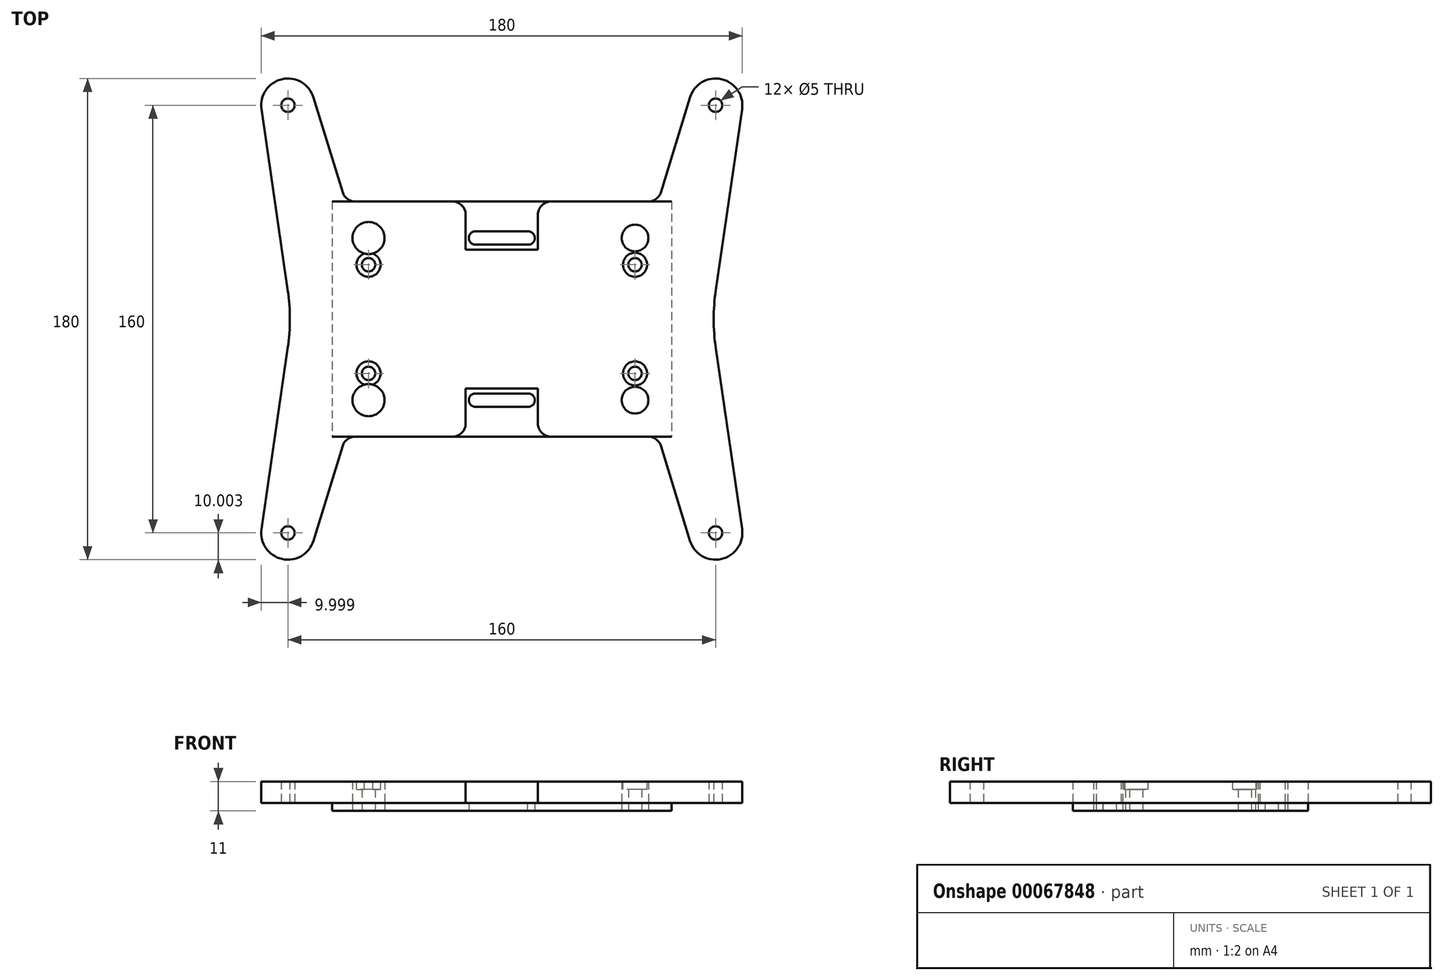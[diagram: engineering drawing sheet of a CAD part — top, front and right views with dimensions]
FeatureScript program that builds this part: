
annotation { "Feature Type Name" : "Feature", "Feature Type Description" : "" }
export const myFeature = defineFeature(function(context is Context, id is Id, definition is map)
    precondition{}
    {
        {
            var Q0;
            Q0=qCreatedBy(makeId("Top.planeOp"),FACE);
            var sketch = newSketch(context, id + "F0", { "sketchPlane" : qUnion([Q0])});
            skLineSegment(sketch, "E0.bottom", {"start": v(-92.69, 30.95) * mm, "end": v(34.32, 30.95) * mm});
            skLineSegment(sketch, "E0.top", {"start": v(-92.69, -57.05) * mm, "end": v(34.32, -57.05) * mm});
            skLineSegment(sketch, "E0.left", {"start": v(-92.69, 30.95) * mm, "end": v(-92.69, -57.05) * mm});
            skLineSegment(sketch, "E0.right", {"start": v(34.32, 30.95) * mm, "end": v(34.32, -57.05) * mm});
            skLineSegment(sketch, "E1", {"start": v(-79.03, 30.95) * mm, "end": v(-79.03, -57.05) * mm, "construction": true});
            skLineSegment(sketch, "E2", {"start": v(20.67, 30.95) * mm, "end": v(20.67, -57.05) * mm, "construction": true});
            skLineSegment(sketch, "E3", {"start": v(-92.69, 17.28) * mm, "end": v(34.32, 17.28) * mm, "construction": true});
            skLineSegment(sketch, "E4", {"start": v(-92.69, -43.37) * mm, "end": v(34.32, -43.37) * mm, "construction": true});
            skLineSegment(sketch, "E5", {"start": v(-92.69, -33.37) * mm, "end": v(34.32, -33.37) * mm, "construction": true});
            skLineSegment(sketch, "E6", {"start": v(-92.69, 7.28) * mm, "end": v(34.32, 7.28) * mm, "construction": true});
            skCircle(sketch, "E7", {"center": v(-79.03, 17.28) * mm, "radius": 6 * mm});
            skCircle(sketch, "E8", {"center": v(20.67, 17.28) * mm, "radius": 5 * mm});
            skCircle(sketch, "E9", {"center": v(20.67, 7.28) * mm, "radius": 2.5 * mm});
            skCircle(sketch, "E10", {"center": v(-79.03, 7.28) * mm, "radius": 2.5 * mm});
            skCircle(sketch, "E11", {"center": v(-79.03, -33.37) * mm, "radius": 2.5 * mm});
            skCircle(sketch, "E12", {"center": v(20.67, -33.37) * mm, "radius": 2.5 * mm});
            skCircle(sketch, "E13", {"center": v(20.67, -43.37) * mm, "radius": 5 * mm});
            skCircle(sketch, "E14", {"center": v(-79.03, -43.37) * mm, "radius": 6 * mm});
            skArc(sketch, "E15", {"start": v(-39.03, -40.87) * mm, "mid": v(-41.53, -43.37) * mm, "end": v(-39.02, -45.87) * mm});
            skArc(sketch, "E16", {"start": v(-19.68, -45.84) * mm, "mid": v(-16.83, -43.54) * mm, "end": v(-19.33, -40.87) * mm});
            skLineSegment(sketch, "E17", {"start": v(-39.03, -40.87) * mm, "end": v(-19.33, -40.87) * mm});
            skLineSegment(sketch, "E18", {"start": v(-18.97, -45.84) * mm, "end": v(-39.02, -45.87) * mm});
            skArc(sketch, "E19", {"start": v(-39.03, 19.78) * mm, "mid": v(-41.53, 17.28) * mm, "end": v(-39.03, 14.78) * mm});
            skArc(sketch, "E20", {"start": v(-19.33, 14.78) * mm, "mid": v(-16.83, 17.28) * mm, "end": v(-19.33, 19.78) * mm});
            skLineSegment(sketch, "E21", {"start": v(-39.03, 19.78) * mm, "end": v(-19.33, 19.78) * mm});
            skLineSegment(sketch, "E22", {"start": v(-39.03, 14.78) * mm, "end": v(-19.33, 14.78) * mm});
            skLineSegment(sketch, "E23", {"start": v(-42.69, 30.95) * mm, "end": v(-42.69, -57.05) * mm, "construction": true});
            skLineSegment(sketch, "E24", {"start": v(-15.68, 30.95) * mm, "end": v(-15.68, -57.05) * mm, "construction": true});
            skLineSegment(sketch, "E25", {"start": v(-42.69, 12.95) * mm, "end": v(-15.68, 12.95) * mm, "construction": true});
            skLineSegment(sketch, "E26", {"start": v(-42.69, -39.05) * mm, "end": v(-15.68, -39.05) * mm, "construction": true});
            skSolve(sketch);
        }
        {
            var Q0;
            Q0=makeQuery(id+"F0.imprint","IMPRINT",FACE,{"disambiguationData":[TD([[makeQuery(id+"F0.imprint","IMPRINT",EDGE,{"derivedFrom":sQuery(id+"F0.wireOp",EDGE,"E0.bottom")}),-1.0]])]});
            extrude(context, id + "F1", {"entities" : qUnion([Q0]), "depth" : 3 * mm});
        }
        {
            var Q0;
            Q0=makeQuery(id+"F1.opExtrude","CAP_FACE",FACE,{"disambiguationData":[OSD([sQuery(id+"F0.wireOp",EDGE,"E0.bottom"),sQuery(id+"F0.wireOp",EDGE,"E0.top"),sQuery(id+"F0.wireOp",EDGE,"E0.left"),sQuery(id+"F0.wireOp",EDGE,"E0.right"),sQuery(id+"F0.wireOp",EDGE,"E7"),sQuery(id+"F0.wireOp",EDGE,"E8"),sQuery(id+"F0.wireOp",EDGE,"E9"),sQuery(id+"F0.wireOp",EDGE,"E10"),sQuery(id+"F0.wireOp",EDGE,"E11"),sQuery(id+"F0.wireOp",EDGE,"E12"),sQuery(id+"F0.wireOp",EDGE,"E13"),sQuery(id+"F0.wireOp",EDGE,"E14"),sQuery(id+"F0.wireOp",EDGE,"E15"),sQuery(id+"F0.wireOp",EDGE,"E16"),sQuery(id+"F0.wireOp",EDGE,"E17"),sQuery(id+"F0.wireOp",EDGE,"E18"),sQuery(id+"F0.wireOp",EDGE,"E19"),sQuery(id+"F0.wireOp",EDGE,"E20"),sQuery(id+"F0.wireOp",EDGE,"E21"),sQuery(id+"F0.wireOp",EDGE,"E22")])],"isStart":false});
            var sketch = newSketch(context, id + "F2", { "sketchPlane" : qUnion([Q0])});
            skLineSegment(sketch, "E27.0", {"start": v(-92.69, 30.95) * mm, "end": v(34.32, 30.95) * mm});
            skLineSegment(sketch, "E27.1", {"start": v(-92.69, 30.95) * mm, "end": v(-92.69, -57.05) * mm});
            skLineSegment(sketch, "E27.2", {"start": v(34.32, 30.95) * mm, "end": v(34.32, -57.05) * mm});
            skLineSegment(sketch, "E27.3", {"start": v(-92.69, -57.05) * mm, "end": v(34.32, -57.05) * mm});
            skCircle(sketch, "E27.4", {"center": v(-79.03, -43.37) * mm, "radius": 6 * mm});
            skCircle(sketch, "E27.5", {"center": v(-79.03, -33.37) * mm, "radius": 2.5 * mm});
            skCircle(sketch, "E27.6", {"center": v(-79.03, 7.28) * mm, "radius": 2.5 * mm});
            skCircle(sketch, "E27.7", {"center": v(-79.03, 17.28) * mm, "radius": 6 * mm});
            skCircle(sketch, "E27.8", {"center": v(20.67, 17.28) * mm, "radius": 5 * mm});
            skCircle(sketch, "E27.9", {"center": v(20.67, 7.28) * mm, "radius": 2.5 * mm});
            skCircle(sketch, "E27.10", {"center": v(20.67, -33.37) * mm, "radius": 2.5 * mm});
            skCircle(sketch, "E27.11", {"center": v(20.67, -43.37) * mm, "radius": 5 * mm});
            skLineSegment(sketch, "E28.bottom", {"start": v(-42.69, 30.95) * mm, "end": v(-15.68, 30.95) * mm});
            skLineSegment(sketch, "E28.top", {"start": v(-42.69, 12.95) * mm, "end": v(-15.68, 12.95) * mm});
            skLineSegment(sketch, "E28.left", {"start": v(-42.69, 30.95) * mm, "end": v(-42.69, 12.95) * mm});
            skLineSegment(sketch, "E28.right", {"start": v(-15.68, 30.95) * mm, "end": v(-15.68, 12.95) * mm});
            skLineSegment(sketch, "E29.bottom", {"start": v(-15.68, -57.05) * mm, "end": v(-42.69, -57.05) * mm});
            skLineSegment(sketch, "E29.top", {"start": v(-15.68, -39.05) * mm, "end": v(-42.69, -39.05) * mm});
            skLineSegment(sketch, "E29.left", {"start": v(-15.68, -57.05) * mm, "end": v(-15.68, -39.05) * mm});
            skLineSegment(sketch, "E29.right", {"start": v(-42.69, -57.05) * mm, "end": v(-42.69, -39.05) * mm});
            skLineSegment(sketch, "E30", {"start": v(-29.18, 30.95) * mm, "end": v(-29.18, -57.05) * mm, "construction": true});
            skLineSegment(sketch, "E31", {"start": v(-92.69, -13.05) * mm, "end": v(34.32, -13.05) * mm, "construction": true});
            skLineSegment(sketch, "E32.rect.bottom", {"start": v(50.82, 66.95) * mm, "end": v(-109.18, 66.95) * mm, "construction": true});
            skLineSegment(sketch, "E32.rect.top", {"start": v(50.82, -93.05) * mm, "end": v(-109.18, -93.05) * mm, "construction": true});
            skLineSegment(sketch, "E32.rect.left", {"start": v(50.82, 66.95) * mm, "end": v(50.82, -93.05) * mm, "construction": true});
            skLineSegment(sketch, "E32.rect.right", {"start": v(-109.18, 66.95) * mm, "end": v(-109.18, -93.05) * mm, "construction": true});
            skPoint(sketch, "E32.rect.middle", {"position": v(-29.18, -13.05) * mm});
            skArc(sketch, "E33", {"start": v(-99.62, 69.88) * mm, "mid": v(-111.37, 76.71) * mm, "end": v(-119.08, 65.52) * mm});
            skArc(sketch, "E34", {"start": v(60.72, 65.52) * mm, "mid": v(53, 76.71) * mm, "end": v(41.26, 69.88) * mm});
            skArc(sketch, "E35", {"start": v(41.26, -95.98) * mm, "mid": v(53, -102.8) * mm, "end": v(60.72, -91.61) * mm});
            skArc(sketch, "E36", {"start": v(-119.08, -91.61) * mm, "mid": v(-111.37, -102.8) * mm, "end": v(-99.62, -95.98) * mm});
            skLineSegment(sketch, "E37", {"start": v(29.32, 30.95) * mm, "end": v(29.32, -57.05) * mm, "construction": true});
            skLineSegment(sketch, "E38", {"start": v(-87.69, 30.95) * mm, "end": v(-87.69, -57.05) * mm, "construction": true});
            skLineSegment(sketch, "E39", {"start": v(-87.69, -57.05) * mm, "end": v(-99.62, -95.98) * mm});
            skLineSegment(sketch, "E40", {"start": v(-87.69, 30.95) * mm, "end": v(-99.62, 69.88) * mm});
            skLineSegment(sketch, "E41", {"start": v(29.32, 30.95) * mm, "end": v(41.26, 69.88) * mm});
            skLineSegment(sketch, "E42", {"start": v(29.32, -57.05) * mm, "end": v(41.26, -95.98) * mm});
            skCircle(sketch, "E43", {"center": v(-109.18, 66.95) * mm, "radius": 2.5 * mm});
            skCircle(sketch, "E44", {"center": v(50.82, 66.95) * mm, "radius": 2.5 * mm});
            skCircle(sketch, "E45", {"center": v(50.82, -93.05) * mm, "radius": 2.5 * mm});
            skCircle(sketch, "E46", {"center": v(-109.18, -93.05) * mm, "radius": 2.5 * mm});
            skLineSegment(sketch, "E47", {"start": v(34.32, -13.05) * mm, "end": v(50.82, -13.05) * mm, "construction": true});
            skLineSegment(sketch, "E48", {"start": v(-92.69, -13.05) * mm, "end": v(-109.18, -13.05) * mm, "construction": true});
            skLineSegment(sketch, "E49", {"start": v(-107.69, 66.95) * mm, "end": v(-107.69, -93.05) * mm, "construction": true});
            skLineSegment(sketch, "E50", {"start": v(49.32, 66.95) * mm, "end": v(49.32, -93.05) * mm, "construction": true});
            skLineSegment(sketch, "E51", {"start": v(49.32, -13.05) * mm, "end": v(60.72, 65.52) * mm});
            skLineSegment(sketch, "E52", {"start": v(49.32, -13.05) * mm, "end": v(60.72, -91.61) * mm});
            skLineSegment(sketch, "E53", {"start": v(-107.69, -13.05) * mm, "end": v(-119.08, 65.52) * mm});
            skLineSegment(sketch, "E54", {"start": v(-107.69, -13.05) * mm, "end": v(-119.08, -91.61) * mm});
            skSolve(sketch);
        }
        {
            var Q0;
            Q0=makeQuery(id+"F2.imprint","IMPRINT",FACE,{"disambiguationData":[TD([[makeQuery(id+"F2.imprint","IMPRINT",EDGE,{"derivedFrom":sQuery(id+"F2.wireOp",EDGE,"E33")}),1.0]])]});
            var Q1;
            Q1=makeQuery(id+"F2.imprint","IMPRINT",FACE,{"disambiguationData":[TD([[makeQuery(id+"F2.imprint","IMPRINT",EDGE,{"derivedFrom":sQuery(id+"F2.wireOp",EDGE,"E36")}),1.0]])]});
            var Q2;
            Q2=makeQuery(id+"F2.imprint","IMPRINT",FACE,{"disambiguationData":[TD([[makeQuery(id+"F2.imprint","IMPRINT",EDGE,{"derivedFrom":sQuery(id+"F2.wireOp",EDGE,"E35")}),1.0]])]});
            var Q3;
            Q3=makeQuery(id+"F2.imprint","IMPRINT",FACE,{"disambiguationData":[TD([[makeQuery(id+"F2.imprint","IMPRINT",EDGE,{"derivedFrom":sQuery(id+"F2.wireOp",EDGE,"E34")}),1.0]])]});
            var Q4;
            Q4=makeQuery(id+"F2.imprint","IMPRINT",FACE,{"disambiguationData":[TD([[makeQuery(id+"F2.imprint","IMPRINT",EDGE,{"derivedFrom":sQuery(id+"F2.wireOp",EDGE,"E27.4")}),-1.0]])]});
            extrude(context, id + "F3", {"entities" : qUnion([Q0, Q1, Q2, Q3, Q4]), "depth" : 8 * mm});
        }
        {
            var Q0;
            Q0=makeQuery(id+"F3.opExtrude","SWEPT_EDGE",EDGE,{"disambiguationData":[OSD([sQuery(id+"F2.wireOp",EDGE,"E53"),sQuery(id+"F2.wireOp",EDGE,"E54")])]});
            var Q1;
            Q1=makeQuery(id+"F3.opExtrude","SWEPT_EDGE",EDGE,{"disambiguationData":[OSD([sQuery(id+"F2.wireOp",EDGE,"E51"),sQuery(id+"F2.wireOp",EDGE,"E52")])]});
            fillet(context, id + "F4", {"entities" : qUnion([Q0, Q1]), "radius" : 75 * mm, "tangentPropagation" : true, "allowEdgeOverflow" : false});
        }
        {
            var Q0;
            Q0=makeQuery(id+"F3.opExtrude","SWEPT_EDGE",EDGE,{"disambiguationData":[OSD([sQuery(id+"F2.wireOp",EDGE,"E27.3"),sQuery(id+"F2.wireOp",EDGE,"E42")])]});
            var Q1;
            Q1=makeQuery(id+"F3.opExtrude","SWEPT_EDGE",EDGE,{"disambiguationData":[OSD([sQuery(id+"F2.wireOp",EDGE,"E27.0"),sQuery(id+"F2.wireOp",EDGE,"E40")])]});
            var Q2;
            Q2=makeQuery(id+"F3.opExtrude","SWEPT_EDGE",EDGE,{"disambiguationData":[OSD([sQuery(id+"F2.wireOp",EDGE,"E27.0"),sQuery(id+"F2.wireOp",EDGE,"E41")])]});
            var Q3;
            Q3=makeQuery(id+"F3.opExtrude","SWEPT_EDGE",EDGE,{"disambiguationData":[OSD([sQuery(id+"F2.wireOp",EDGE,"E27.3"),sQuery(id+"F2.wireOp",EDGE,"E39")])]});
            fillet(context, id + "F5", {"entities" : qUnion([Q0, Q1, Q2, Q3]), "radius" : 5 * mm, "tangentPropagation" : true, "allowEdgeOverflow" : false});
        }
        {
            var Q0;
            Q0=makeQuery(id+"F3.opExtrude","SWEPT_EDGE",EDGE,{"disambiguationData":[OSD([sQuery(id+"F2.wireOp",EDGE,"E27.3"),sQuery(id+"F2.wireOp",EDGE,"E29.bottom"),sQuery(id+"F2.wireOp",EDGE,"E29.right")])]});
            var Q1;
            Q1=makeQuery(id+"F3.opExtrude","SWEPT_EDGE",EDGE,{"disambiguationData":[OSD([sQuery(id+"F2.wireOp",EDGE,"E27.3"),sQuery(id+"F2.wireOp",EDGE,"E29.bottom"),sQuery(id+"F2.wireOp",EDGE,"E29.left")])]});
            var Q2;
            Q2=makeQuery(id+"F3.opExtrude","SWEPT_EDGE",EDGE,{"disambiguationData":[OSD([sQuery(id+"F2.wireOp",EDGE,"E27.0"),sQuery(id+"F2.wireOp",EDGE,"E28.bottom"),sQuery(id+"F2.wireOp",EDGE,"E28.left")])]});
            var Q3;
            Q3=makeQuery(id+"F3.opExtrude","SWEPT_EDGE",EDGE,{"disambiguationData":[OSD([sQuery(id+"F2.wireOp",EDGE,"E27.0"),sQuery(id+"F2.wireOp",EDGE,"E28.bottom"),sQuery(id+"F2.wireOp",EDGE,"E28.right")])]});
            fillet(context, id + "F6", {"entities" : qUnion([Q0, Q1, Q2, Q3]), "radius" : 5 * mm, "tangentPropagation" : true, "allowEdgeOverflow" : false});
        }
        {
            var Q0;
            Q0=makeQuery(id+"F3.opExtrude","CAP_FACE",FACE,{"disambiguationData":[OSD([sQuery(id+"F2.wireOp",EDGE,"E27.0"),sQuery(id+"F2.wireOp",EDGE,"E27.3"),sQuery(id+"F2.wireOp",EDGE,"E27.4"),sQuery(id+"F2.wireOp",EDGE,"E27.5"),sQuery(id+"F2.wireOp",EDGE,"E27.6"),sQuery(id+"F2.wireOp",EDGE,"E27.7"),sQuery(id+"F2.wireOp",EDGE,"E27.8"),sQuery(id+"F2.wireOp",EDGE,"E27.9"),sQuery(id+"F2.wireOp",EDGE,"E27.10"),sQuery(id+"F2.wireOp",EDGE,"E27.11"),sQuery(id+"F2.wireOp",EDGE,"E28.top"),sQuery(id+"F2.wireOp",EDGE,"E28.left"),sQuery(id+"F2.wireOp",EDGE,"E28.right"),sQuery(id+"F2.wireOp",EDGE,"E29.top"),sQuery(id+"F2.wireOp",EDGE,"E29.left"),sQuery(id+"F2.wireOp",EDGE,"E29.right"),sQuery(id+"F2.wireOp",EDGE,"E33"),sQuery(id+"F2.wireOp",EDGE,"E34"),sQuery(id+"F2.wireOp",EDGE,"E35"),sQuery(id+"F2.wireOp",EDGE,"E36"),sQuery(id+"F2.wireOp",EDGE,"E39"),sQuery(id+"F2.wireOp",EDGE,"E40"),sQuery(id+"F2.wireOp",EDGE,"E41"),sQuery(id+"F2.wireOp",EDGE,"E42"),sQuery(id+"F2.wireOp",EDGE,"E43"),sQuery(id+"F2.wireOp",EDGE,"E44"),sQuery(id+"F2.wireOp",EDGE,"E45"),sQuery(id+"F2.wireOp",EDGE,"E46"),sQuery(id+"F2.wireOp",EDGE,"E51"),sQuery(id+"F2.wireOp",EDGE,"E52"),sQuery(id+"F2.wireOp",EDGE,"E53"),sQuery(id+"F2.wireOp",EDGE,"E54")])],"isStart":false});
            var sketch = newSketch(context, id + "F7", { "sketchPlane" : qUnion([Q0])});
            skCircle(sketch, "E55.0", {"center": v(-79.03, 7.28) * mm, "radius": 2.5 * mm});
            skCircle(sketch, "E56.0", {"center": v(20.67, 7.28) * mm, "radius": 2.5 * mm});
            skCircle(sketch, "E57.0", {"center": v(20.67, -33.37) * mm, "radius": 2.5 * mm});
            skCircle(sketch, "E58.0", {"center": v(-79.03, -33.37) * mm, "radius": 2.5 * mm});
            skCircle(sketch, "E59", {"center": v(-79.03, 7.28) * mm, "radius": 4.5 * mm});
            skCircle(sketch, "E60", {"center": v(20.67, 7.28) * mm, "radius": 4.5 * mm});
            skCircle(sketch, "E61", {"center": v(20.67, -33.37) * mm, "radius": 4.5 * mm});
            skCircle(sketch, "E62", {"center": v(-79.03, -33.37) * mm, "radius": 4.5 * mm});
            skSolve(sketch);
        }
        {
            var Q0;
            Q0=makeQuery(id+"F7.imprint","IMPRINT",FACE,{"disambiguationData":[TD([[makeQuery(id+"F7.imprint","IMPRINT",EDGE,{"derivedFrom":sQuery(id+"F7.wireOp",EDGE,"E56.0")}),-1.0]])]});
            var Q1;
            Q1=makeQuery(id+"F7.imprint","IMPRINT",FACE,{"disambiguationData":[TD([[makeQuery(id+"F7.imprint","IMPRINT",EDGE,{"derivedFrom":sQuery(id+"F7.wireOp",EDGE,"E57.0")}),-1.0]])]});
            var Q2;
            Q2=makeQuery(id+"F7.imprint","IMPRINT",FACE,{"disambiguationData":[TD([[makeQuery(id+"F7.imprint","IMPRINT",EDGE,{"derivedFrom":sQuery(id+"F7.wireOp",EDGE,"E58.0")}),-1.0]])]});
            var Q3;
            Q3=makeQuery(id+"F7.imprint","IMPRINT",FACE,{"disambiguationData":[TD([[makeQuery(id+"F7.imprint","IMPRINT",EDGE,{"derivedFrom":sQuery(id+"F7.wireOp",EDGE,"E55.0")}),-1.0]])]});
            extrude(context, id + "F8", {"entities" : qUnion([Q0, Q1, Q2, Q3]), "operationType" : NewBodyOperationType.REMOVE, "oppositeDirection" : true, "depth" : 3 * mm});
        }
    });
